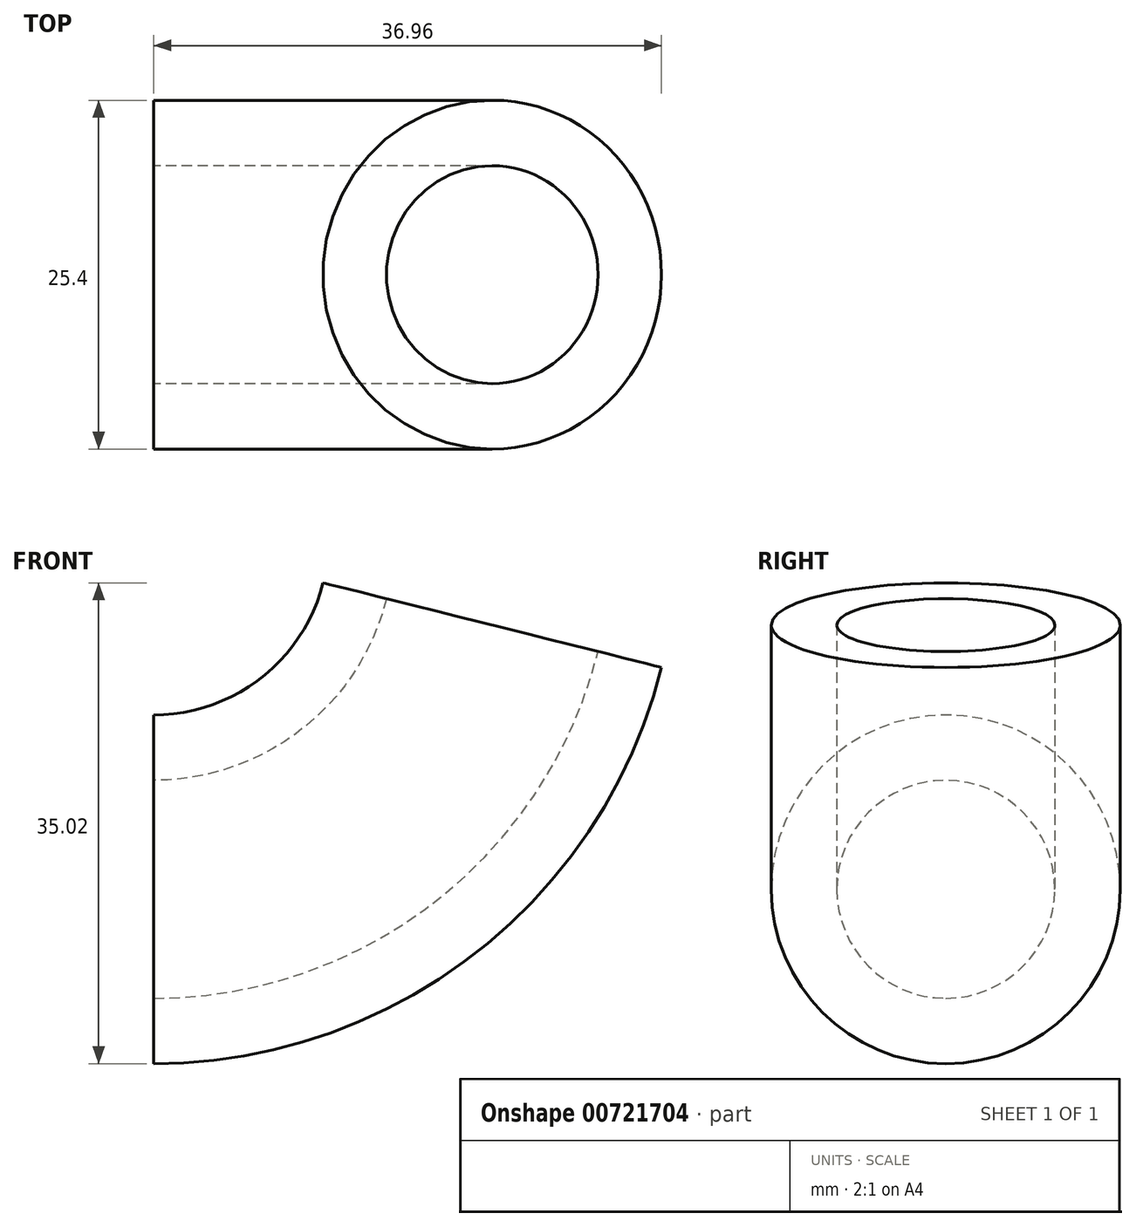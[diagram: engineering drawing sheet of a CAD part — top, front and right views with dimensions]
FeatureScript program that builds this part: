
annotation { "Feature Type Name" : "Feature", "Feature Type Description" : "" }
export const myFeature = defineFeature(function(context is Context, id is Id, definition is map)
    precondition{}
    {
        {
            var Q0;
            Q0=qCreatedBy(makeId("Front.planeOp"),FACE);
            var sketch = newSketch(context, id + "F0", { "sketchPlane" : qUnion([Q0])});
            skPoint(sketch, "E0.visualSharp", {"position": v(4518.56, 0) * mm});
            skPoint(sketch, "E1.orphan", {"position": v(-4518.56, 0) * mm});
            skArc(sketch, "E2.filletArc", {"start": v(0, 0) * mm, "mid": v(15.63, 5.38) * mm, "end": v(24.64, 19.24) * mm});
            skSolve(sketch);
        }
        {
            var Q0;
            Q0=qCreatedBy(makeId("Right.planeOp"),FACE);
            var sketch = newSketch(context, id + "F1", { "sketchPlane" : qUnion([Q0])});
            skCircle(sketch, "E3", {"center": v(0, 0) * mm, "radius": 12.7 * mm});
            skCircle(sketch, "E4", {"center": v(0, 0) * mm, "radius": 7.94 * mm});
            skSolve(sketch);
        }
        {
            var Q0;
            Q0=qSketchRegion(id+"F1",true);
            var Q1;
            Q1=qConstructionFilter(qBodyType(qCreatedBy(id+"F0",EDGE),BodyType.WIRE),ConstructionObject.NO);
            sweep(context, id + "F2", {"profiles" : qUnion([Q0]), "path" : qUnion([Q1])});
        }
    });
